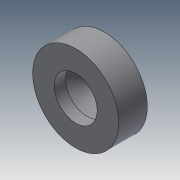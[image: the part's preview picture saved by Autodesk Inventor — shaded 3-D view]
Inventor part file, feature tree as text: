
AUTODESK INVENTOR PART (.ipt)
format: ipt  version: 2018.3 (Build 223284000, 284)  size: 112,128 bytes
history: native  units: in
note: dims shown in document units (in); Inventor stores cm internally (conversion verified against a paired STEP export)
features: extrude x2, sketch x2, hole x1
ambient origin geometry x8: Origin, YZ Plane, XZ Plane, XY Plane, X Axis, Y Axis, Z Axis, Center Point
bodies: Solid1 (feature_tree)
feature tree (5):
  extrude  "Extrusion1"  Depth=0.25in TaperAngle=0.0deg
  extrude  "Extrusion2"  Depth=0.375in TaperAngle=0.0deg
  hole  "Hole1"  [1 undecoded]
  sketch  "Sketch1"  dims[d0=0.75in d1=0.25in d2=0.0in]
  sketch  "Sketch2"  dims[d3=0.375in d4=0.1in d5=0.0in d6=1.0in d7=1.0in d8=0.177in d9=0.75in d10=0.375in d11=0.188in d12=0.5635in d13=1.0in d14=0.8108in]
note: 1 required parameter value undecoded (feature->parameter linkage not recoverable at this tier; creation-order binding heuristic only, values carry confidence <= 0.55)
